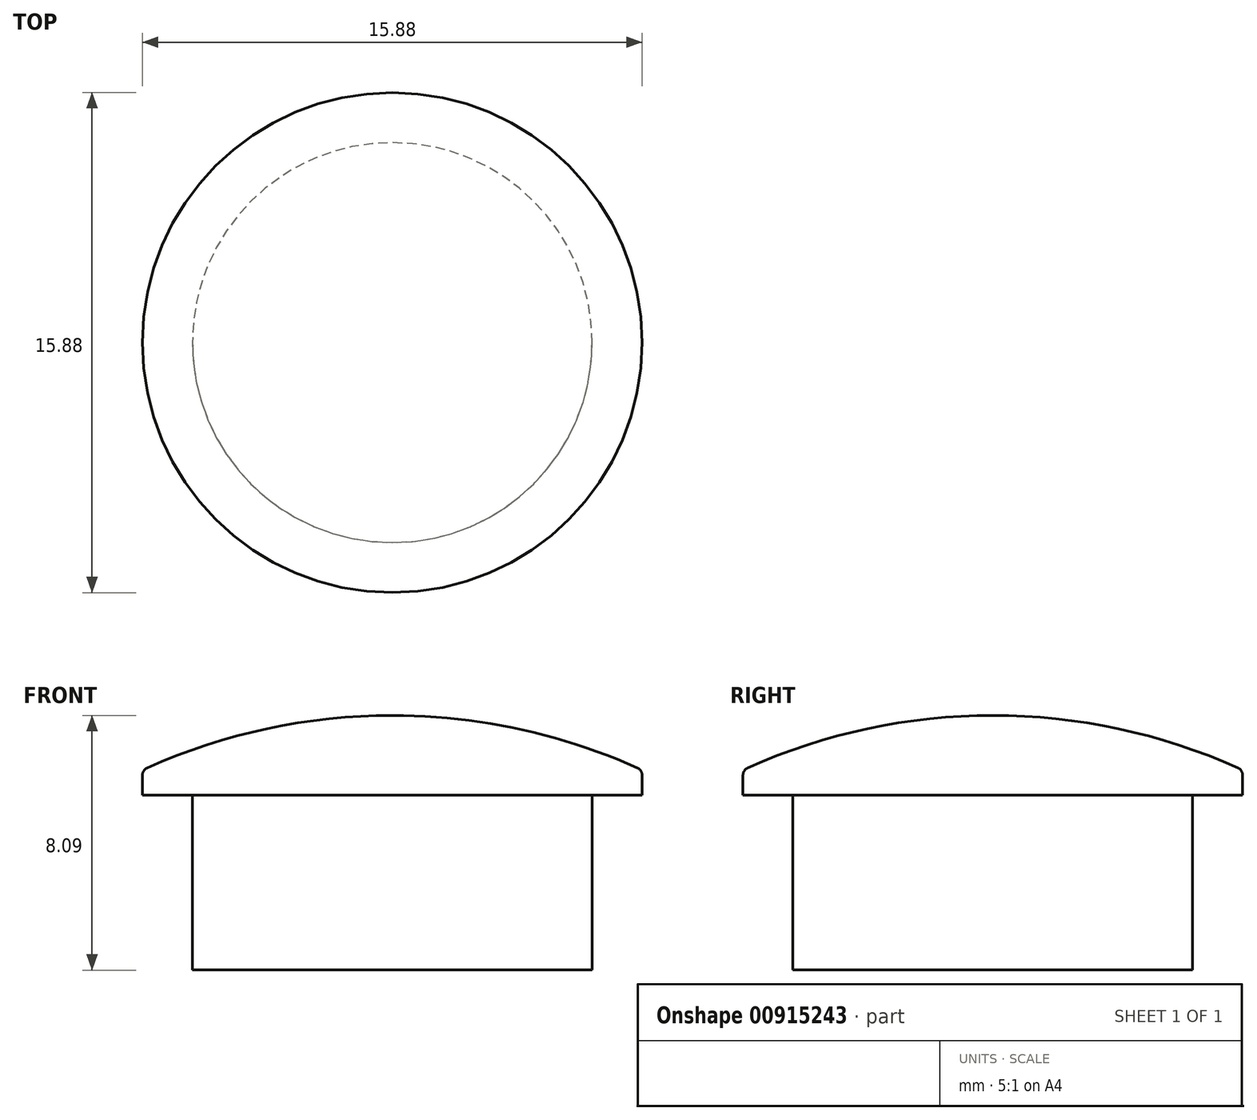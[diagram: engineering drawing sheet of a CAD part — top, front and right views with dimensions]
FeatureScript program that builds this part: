
annotation { "Feature Type Name" : "Feature", "Feature Type Description" : "" }
export const myFeature = defineFeature(function(context is Context, id is Id, definition is map)
    precondition{}
    {
        {
            var Q0;
            Q0=qCreatedBy(makeId("Top.planeOp"),FACE);
            var sketch = newSketch(context, id + "F0", { "sketchPlane" : qUnion([Q0])});
            skCircle(sketch, "E0", {"center": v(0, 0) * mm, "radius": 6.35 * mm});
            skSolve(sketch);
        }
        {
            var Q0;
            Q0 = qSketchRegion(id + "F0", true);
            extrude(context, id + "F1", {"entities" : qUnion([Q0]), "endBound" : BoundingType.SYMMETRIC, "depth" : 6.35 * mm, "offsetDistance" : 25.4 * mm});
        }
        {
            var Q0;
            Q0=qCreatedBy(makeId("Front.planeOp"),FACE);
            var sketch = newSketch(context, id + "F2", { "sketchPlane" : qUnion([Q0])});
            skArc(sketch, "E1", {"start": v(7.94, 3.18) * mm, "mid": v(4.06, 4.47) * mm, "end": v(0, 4.9) * mm});
            skLineSegment(sketch, "E2", {"start": v(0, 2.38) * mm, "end": v(0, 4.9) * mm});
            skLineSegment(sketch, "E3", {"start": v(0, 2.38) * mm, "end": v(7.94, 2.38) * mm});
            skLineSegment(sketch, "E4", {"start": v(7.94, 2.38) * mm, "end": v(7.94, 3.18) * mm});
            skPoint(sketch, "E5.orphan", {"position": v(0, 2.38) * mm});
            skPoint(sketch, "E6.start.orphan", {"position": v(6.35, 3.18) * mm});
            skSolve(sketch);
        }
        {
            var Q0;
            Q0=qCreatedBy(makeId("Front.planeOp"),FACE);
            var sketch = newSketch(context, id + "F3", { "sketchPlane" : qUnion([Q0])});
            skLineSegment(sketch, "E7.0", {"start": v(0, 2.38) * mm, "end": v(0, 5.7) * mm});
            skLineSegment(sketch, "E8.0", {"start": v(0, 2.38) * mm, "end": v(8.73, 2.38) * mm});
            skArc(sketch, "E9.0", {"start": v(8.73, 3.68) * mm, "mid": v(4.48, 5.19) * mm, "end": v(0, 5.7) * mm});
            skLineSegment(sketch, "E9.1", {"start": v(8.73, 2.38) * mm, "end": v(8.73, 3.68) * mm});
            skPoint(sketch, "E10.orphan", {"position": v(0, 4.9) * mm});
            skPoint(sketch, "E11.orphan", {"position": v(7.94, 2.38) * mm});
            skSolve(sketch);
        }
        {
            var Q0;
            Q0 = qSketchRegion(id + "F2", true);
            var Q1;
            Q1=sQuery(id+"F2.wireOp",EDGE,"E2");
            revolve(context, id + "F4", {"operationType" : NewBodyOperationType.ADD, "surfaceOperationType" : NewSurfaceOperationType.NEW, "entities" : qUnion([Q0]), "axis" : qUnion([Q1]), "revolveType" : RevolveType.FULL});
        }
        {
            var Q0;
            Q0=makeQuery(id+"F4.opRevolve","SWEPT_EDGE",EDGE,{"disambiguationData":[OSD([sQuery(id+"F2.wireOp",EDGE,"E1"),sQuery(id+"F2.wireOp",EDGE,"E4")])]});
            fillet(context, id + "F5", {"entities" : qUnion([Q0]), "radius" : 0.25 * mm, "tangentPropagation" : true, "allowEdgeOverflow" : false});
        }
    });
